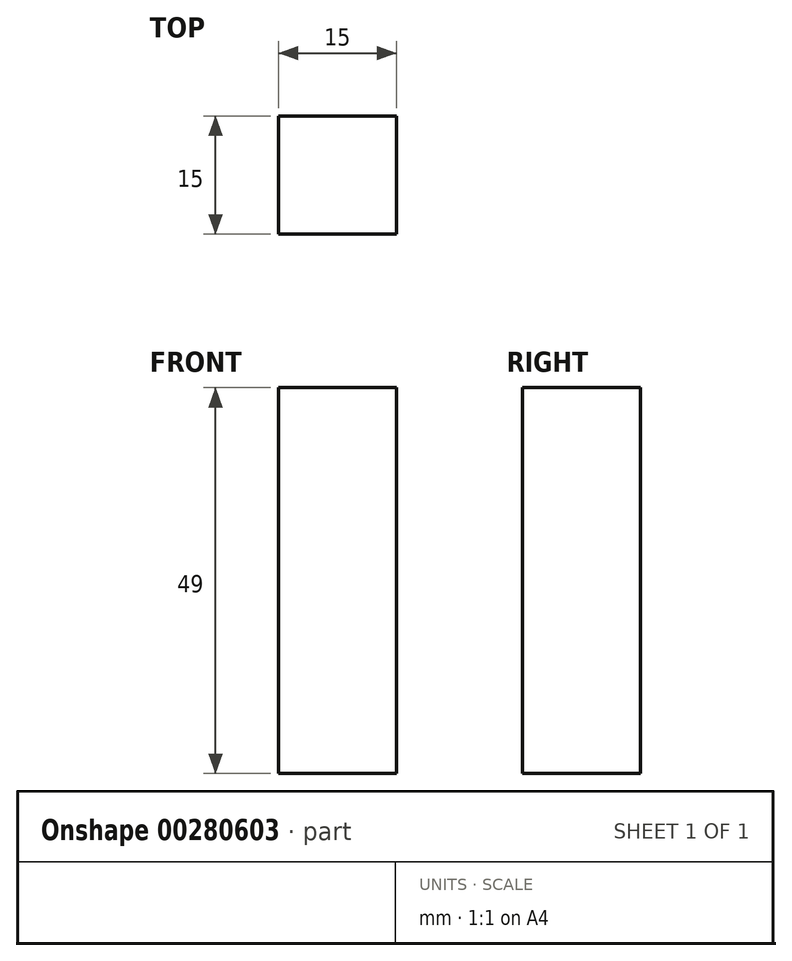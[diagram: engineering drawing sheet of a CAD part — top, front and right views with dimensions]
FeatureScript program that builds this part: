
annotation { "Feature Type Name" : "Feature", "Feature Type Description" : "" }
export const myFeature = defineFeature(function(context is Context, id is Id, definition is map)
    precondition{}
    {
        {
            var Q0;
            Q0=qCreatedBy(makeId("Top.planeOp"),FACE);
            var sketch = newSketch(context, id + "F0", { "sketchPlane" : qUnion([Q0])});
            skLineSegment(sketch, "E0.bottom", {"start": v(0, 7.5) * mm, "end": v(15, 7.5) * mm});
            skLineSegment(sketch, "E0.top", {"start": v(0, -7.5) * mm, "end": v(15, -7.5) * mm});
            skLineSegment(sketch, "E0.left", {"start": v(0, 7.5) * mm, "end": v(0, -7.5) * mm});
            skLineSegment(sketch, "E0.right", {"start": v(15, 7.5) * mm, "end": v(15, -7.5) * mm});
            skPoint(sketch, "E0.middle", {"position": v(7.5, 0) * mm});
            skSolve(sketch);
        }
        {
            var Q0;
            Q0=makeQuery(id+"F0.imprint","IMPRINT",FACE,{"disambiguationData":[TD([[makeQuery(id+"F0.imprint","IMPRINT",EDGE,{"derivedFrom":sQuery(id+"F0.wireOp",EDGE,"E0.bottom")}),-1.0]])]});
            extrude(context, id + "F1", {"entities" : qUnion([Q0]), "depth" : 49 * mm});
        }
    });
